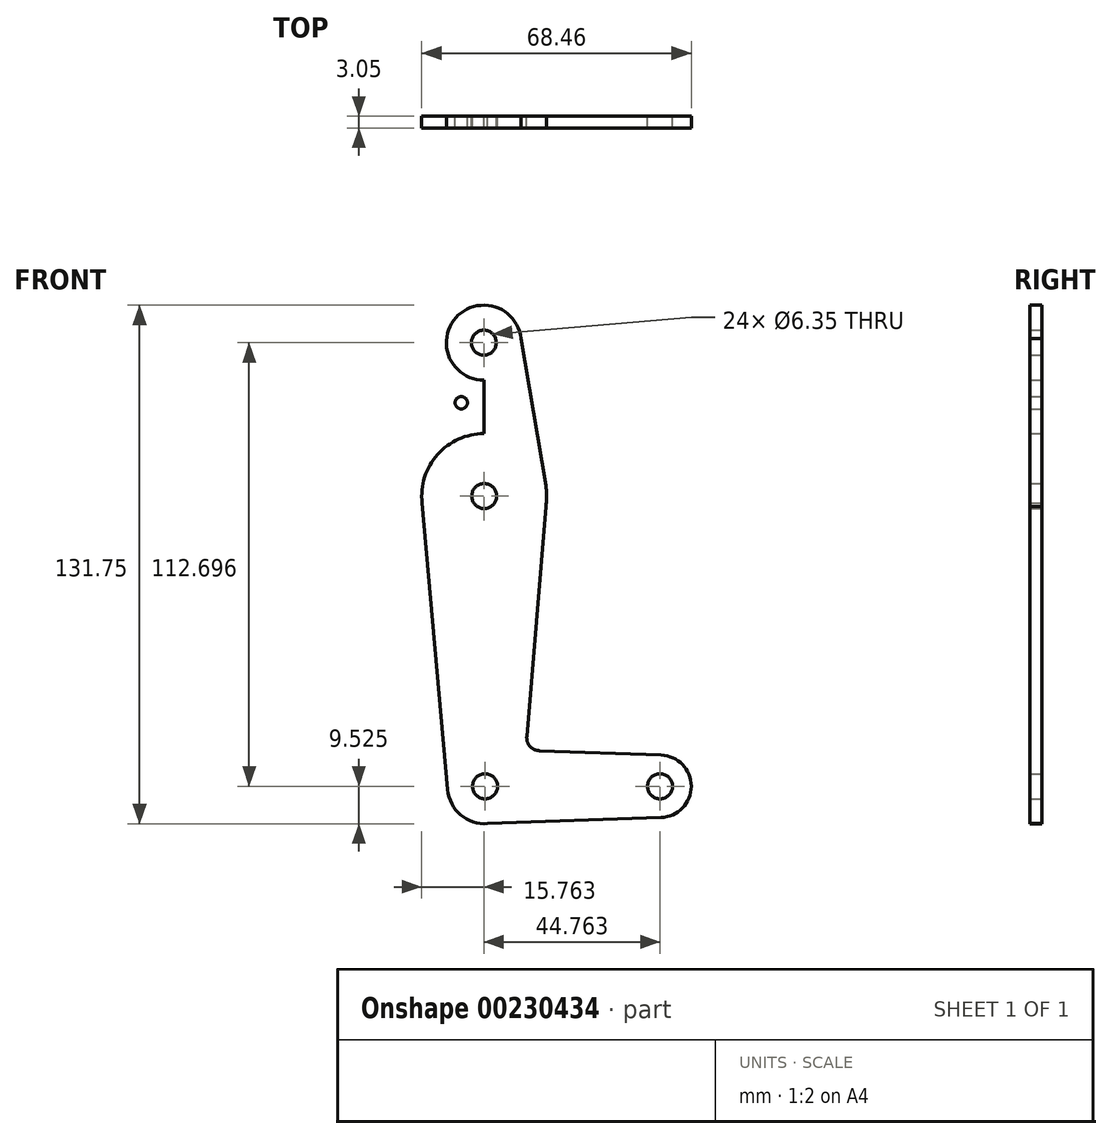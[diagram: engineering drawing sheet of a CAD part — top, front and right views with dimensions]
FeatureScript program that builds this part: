
annotation { "Feature Type Name" : "Feature", "Feature Type Description" : "" }
export const myFeature = defineFeature(function(context is Context, id is Id, definition is map)
    precondition{}
    {
        {
            var Q0;
            Q0=qCreatedBy(makeId("Front.planeOp"),FACE);
            var sketch = newSketch(context, id + "F0", { "sketchPlane" : qUnion([Q0])});
            skCircle(sketch, "E0", {"center": v(-45.2, 102.15) * mm, "radius": 9.53 * mm});
            skCircle(sketch, "E1", {"center": v(-44.88, -10.55) * mm, "radius": 9.53 * mm});
            skLineSegment(sketch, "E2", {"start": v(-45.2, 102.15) * mm, "end": v(-44.88, -10.55) * mm});
            skLineSegment(sketch, "E3", {"start": v(-44.88, -10.55) * mm, "end": v(43.79, -10.55) * mm});
            skCircle(sketch, "E4", {"center": v(-45.2, 102.15) * mm, "radius": 3.18 * mm});
            skCircle(sketch, "E5", {"center": v(-44.88, -10.55) * mm, "radius": 3.18 * mm});
            skCircle(sketch, "E6", {"center": v(-0.43, -10.55) * mm, "radius": 7.94 * mm});
            skLineSegment(sketch, "E7", {"start": v(-44.86, -20.07) * mm, "end": v(-0.15, -18.48) * mm});
            skLineSegment(sketch, "E8", {"start": v(-31.1, -1.51) * mm, "end": v(-0.15, -2.61) * mm});
            skCircle(sketch, "E9", {"center": v(-0.43, -10.55) * mm, "radius": 3.18 * mm});
            skCircle(sketch, "E10", {"center": v(-45.09, 63.18) * mm, "radius": 15.88 * mm});
            skCircle(sketch, "E11", {"center": v(-45.09, 63.18) * mm, "radius": 3.18 * mm});
            skLineSegment(sketch, "E12", {"start": v(-35.74, 103.25) * mm, "end": v(-29.43, 65.82) * mm});
            skLineSegment(sketch, "E13", {"start": v(-54.72, 102) * mm, "end": v(-60.74, 65.82) * mm});
            skLineSegment(sketch, "E14", {"start": v(-60.86, 61.39) * mm, "end": v(-54.37, -11.4) * mm});
            skLineSegment(sketch, "E15", {"start": v(-29.43, 60.55) * mm, "end": v(-34.28, 2.06) * mm});
            skArc(sketch, "E16.filletArc", {"start": v(-34.28, 2.06) * mm, "mid": v(-33.46, -0.4) * mm, "end": v(-31.1, -1.51) * mm});
            skCircle(sketch, "E17", {"center": v(-50.92, 86.9) * mm, "radius": 1.59 * mm});
            skSolve(sketch);
        }
        {
            var Q0;
            Q0 = qSketchRegion(id + "F0", true);
            var Q1;
            {var subQ0=sQuery(id+"F0.wireOp",EDGE,"E2");var subQ1=sQuery(id+"F0.wireOp",EDGE,"E1");var subQ2=makeQuery(id+"F0.imprint","INTERSECT",VERTEX,{"derivedFrom":[subQ1,subQ0]});Q1=makeQuery(id+"F0.imprint","IMPRINT",FACE,{"disambiguationData":[TD([[makeQuery(id+"F0.imprint","IMPRINT",EDGE,{"disambiguationData":[TD([[subQ2,1.0]])],"derivedFrom":subQ1}),1.0]])]});}
            extrude(context, id + "F1", {"entities" : qUnion([Q0, Q1]), "depth" : 3.05 * mm});
        }
    });
